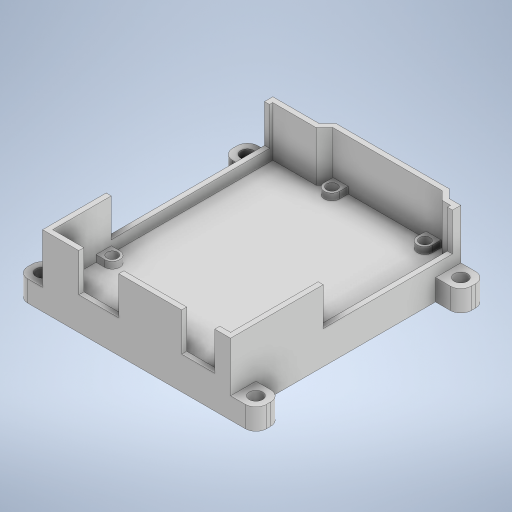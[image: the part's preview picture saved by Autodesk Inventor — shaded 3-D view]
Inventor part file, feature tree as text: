
AUTODESK INVENTOR PART (.ipt)
format: ipt  version: 2024 (Build 280153000, 153)  size: 835,584 bytes
history: native  units: in
note: dims shown in document units (in); Inventor stores cm internally (conversion verified against a paired STEP export)
features: extrude x14, sketch x11, projected_geometry x8
ambient origin geometry x8: Origin, YZ Plane, XZ Plane, XY Plane, X Axis, Y Axis, Z Axis, Center Point
bodies: Solid1 (feature_tree)
feature tree (33):
  extrude  "Extrusion1"  Depth=0.0625in
  extrude  "Extrusion2"  Depth=0.0625in
  extrude  "Extrusion3"  Depth=0.0625in
  extrude  "Extrusion4"  Depth=0.0625in
  extrude  "Extrusion5"  Depth=0.3in
  extrude  "Extrusion6"  Depth=0.3in
  extrude  "Extrusion8"  Depth=0.3in
  sketch  "Sketch6"  dims[d6=0.0625in d7=0.0625in]
  extrude  "Extrusion10"  Depth=0.3in
  extrude  "Extrusion11"  Depth=0.3in
  extrude  "Extrusion12"  Depth=0.1575in
  extrude  "Extrusion13"  Depth=0.125in TaperAngle=0.0deg
  extrude  "Extrusion14"  Depth=0.125in TaperAngle=0.0deg
  extrude  "Extrusion15"  Depth=0.125in TaperAngle=0.0deg
  extrude  "Extrusion16"  TaperAngle=0.0deg  [1 undecoded]
  sketch  "Sketch3"  dims[d0=0.0625in d1=0.0625in]
  projected_geometry  "Projected Loop1"
  sketch  "Sketch4"  dims[d2=0.0625in d3=0.0625in]
  projected_geometry  "Projected Loop2"
  sketch  "Sketch5"  dims[d4=0.0625in d5=0.0625in]
  projected_geometry  "Projected Loop3"
  projected_geometry  "Projected Loop4"
  projected_geometry  "Projected Loop6"
  projected_geometry  "Projected Loop8"
  projected_geometry  "Projected Loop11"
  projected_geometry  "Projected Loop12"
  sketch  "Sketch8"  dims[d8=0.3in d9=0.3in]
  sketch  "Sketch9"  dims[d10=0.1575in d11=0.3in]
  sketch  "Sketch10"  dims[d12=0.3in d13=0.3in]
  sketch  "Sketch11"  dims[d14=0.3in d15=0.3in]
  sketch  "Sketch12"  dims[d16=0.3in d17=0.1575in]
  sketch  "Sketch13"  dims[d18=0.1575in d19=0.1575in]
  sketch  "Sketch14"  dims[d20=0.125in d21=0.125in d22=0.0in d23=0.125in d24=0.0in d25=0.125in d26=0.0in d27=0.0in d28=0.0in d29=0.06in d30=0.5906in d31=0.0in d32=0.0in d33=0.0in d36=0.18in d37=0.18in d38=0.18in d39=0.18in d40=0.0787in d41=0.0in d44=1.0in d45=0.0in d46=0.25in d47=0.0in d48=0.1378in d49=0.0in d50=1.0in d51=0.0in d52=0.45in d53=0.0in d54=0.098in d55=1.0in d56=0.0in d57=0.015in d58=1.0in d59=0.0in]
note: 1 required parameter value undecoded (feature->parameter linkage not recoverable at this tier; creation-order binding heuristic only, values carry confidence <= 0.55)
